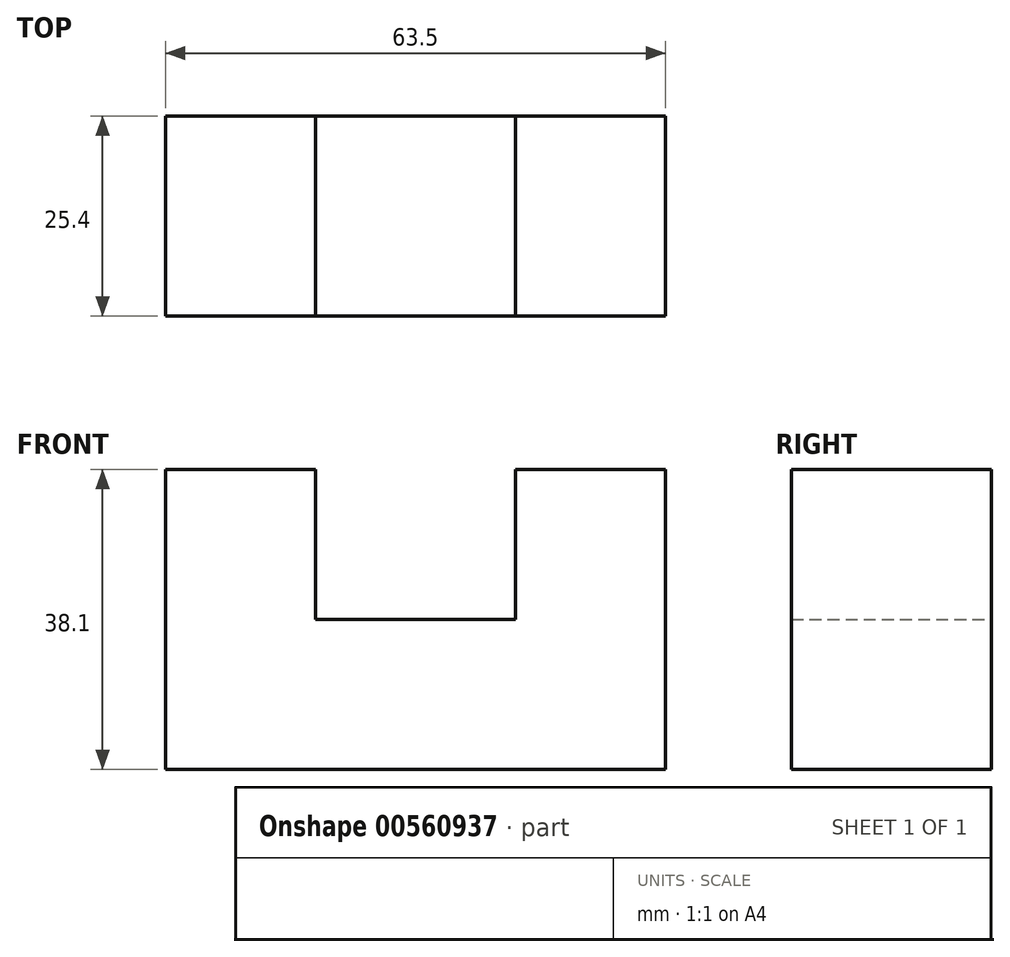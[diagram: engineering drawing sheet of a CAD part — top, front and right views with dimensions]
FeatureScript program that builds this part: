
annotation { "Feature Type Name" : "Feature", "Feature Type Description" : "" }
export const myFeature = defineFeature(function(context is Context, id is Id, definition is map)
    precondition{}
    {
        {
            var Q0;
            Q0=qCreatedBy(makeId("Front.planeOp"),FACE);
            var sketch = newSketch(context, id + "F0", { "sketchPlane" : qUnion([Q0])});
            skLineSegment(sketch, "E0", {"start": v(0, 38.1) * mm, "end": v(0, 0) * mm});
            skLineSegment(sketch, "E1", {"start": v(0, 0) * mm, "end": v(63.5, 0) * mm});
            skLineSegment(sketch, "E2", {"start": v(63.5, 0) * mm, "end": v(63.5, 38.1) * mm});
            skLineSegment(sketch, "E3", {"start": v(63.5, 38.1) * mm, "end": v(44.45, 38.1) * mm});
            skLineSegment(sketch, "E4", {"start": v(44.45, 38.1) * mm, "end": v(44.45, 19.05) * mm});
            skLineSegment(sketch, "E5", {"start": v(44.45, 19.05) * mm, "end": v(19.05, 19.05) * mm});
            skLineSegment(sketch, "E6", {"start": v(19.05, 19.05) * mm, "end": v(19.05, 38.1) * mm});
            skLineSegment(sketch, "E7", {"start": v(19.05, 38.1) * mm, "end": v(0, 38.1) * mm});
            skSolve(sketch);
        }
        {
            var Q0;
            Q0 = qSketchRegion(id + "F0", true);
            extrude(context, id + "F1", {"entities" : qUnion([Q0]), "depth" : 25.4 * mm, "offsetDistance" : 25.4 * mm});
        }
    });
